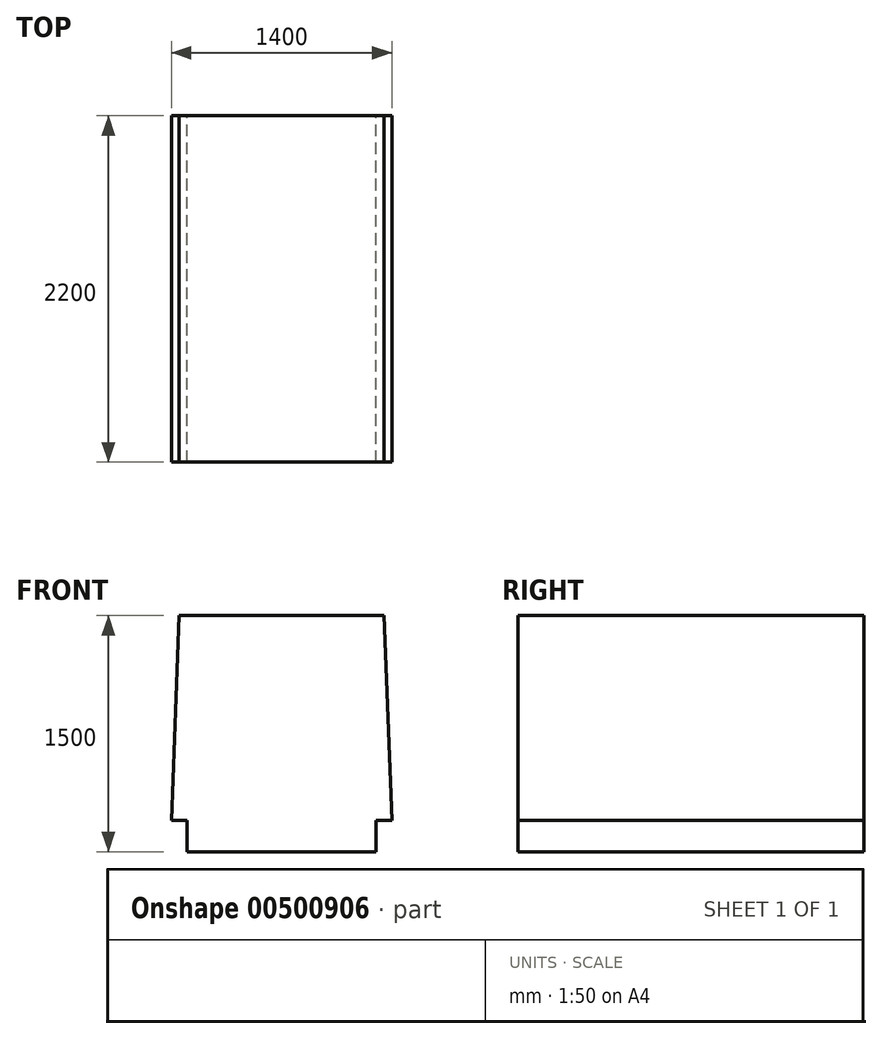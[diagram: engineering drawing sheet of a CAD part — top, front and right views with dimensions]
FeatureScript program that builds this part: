
annotation { "Feature Type Name" : "Feature", "Feature Type Description" : "" }
export const myFeature = defineFeature(function(context is Context, id is Id, definition is map)
    precondition{}
    {
        {
            var Q0;
            Q0=qCreatedBy(makeId("Front.planeOp"),FACE);
            var sketch = newSketch(context, id + "F0", { "sketchPlane" : qUnion([Q0])});
            skLineSegment(sketch, "E0", {"start": v(-600, 0) * mm, "end": v(600, 0) * mm});
            skLineSegment(sketch, "E1", {"start": v(-600, 0) * mm, "end": v(-600, 200) * mm});
            skLineSegment(sketch, "E2", {"start": v(600, 0) * mm, "end": v(600, 200) * mm});
            skLineSegment(sketch, "E3", {"start": v(700, 200) * mm, "end": v(600, 200) * mm});
            skLineSegment(sketch, "E4", {"start": v(650, 1500) * mm, "end": v(700, 200) * mm});
            skLineSegment(sketch, "E5", {"start": v(650, 1500) * mm, "end": v(-650, 1500) * mm});
            skLineSegment(sketch, "E6", {"start": v(-650, 1500) * mm, "end": v(-700, 200) * mm});
            skLineSegment(sketch, "E7", {"start": v(-700, 200) * mm, "end": v(-600, 200) * mm});
            skLineSegment(sketch, "E8", {"start": v(0, 0) * mm, "end": v(0, 1500) * mm, "construction": true});
            skSolve(sketch);
        }
        {
            var Q0;
            Q0=makeQuery(id+"F0.imprint","IMPRINT",FACE,{"disambiguationData":[TD([[makeQuery(id+"F0.imprint","IMPRINT",EDGE,{"derivedFrom":sQuery(id+"F0.wireOp",EDGE,"E0")}),1.0]])]});
            extrude(context, id + "F1", {"entities" : qUnion([Q0]), "depth" : 2200 * mm});
        }
    });
